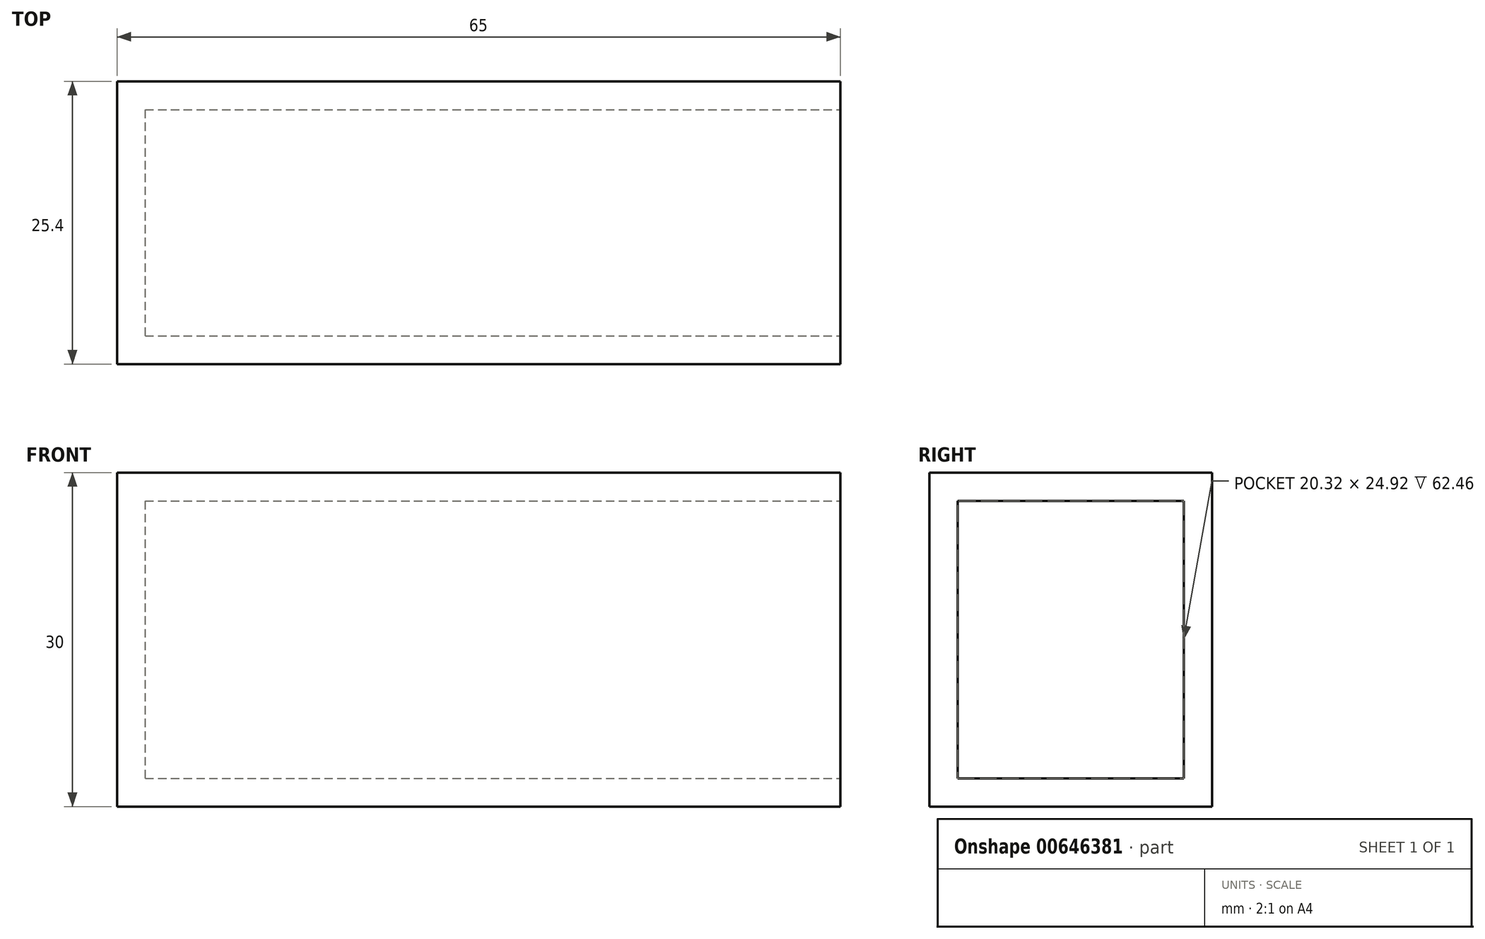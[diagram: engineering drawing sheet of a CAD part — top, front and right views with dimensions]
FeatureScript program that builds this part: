
annotation { "Feature Type Name" : "Feature", "Feature Type Description" : "" }
export const myFeature = defineFeature(function(context is Context, id is Id, definition is map)
    precondition{}
    {
        {
            var Q0;
            Q0=qCreatedBy(makeId("Front.planeOp"),FACE);
            var sketch = newSketch(context, id + "F0", { "sketchPlane" : qUnion([Q0])});
            skLineSegment(sketch, "E0.bottom", {"start": v(-32.5, -15) * mm, "end": v(32.5, -15) * mm});
            skLineSegment(sketch, "E0.top", {"start": v(-32.5, 15) * mm, "end": v(32.5, 15) * mm});
            skLineSegment(sketch, "E0.left", {"start": v(-32.5, -15) * mm, "end": v(-32.5, 15) * mm});
            skLineSegment(sketch, "E0.right", {"start": v(32.5, -15) * mm, "end": v(32.5, 15) * mm});
            skPoint(sketch, "E0.middle", {"position": v(0, 0) * mm});
            skSolve(sketch);
        }
        {
            var Q0;
            Q0=makeQuery(id+"F0.imprint","IMPRINT",FACE,{"disambiguationData":[TD([[makeQuery(id+"F0.imprint","IMPRINT",EDGE,{"derivedFrom":sQuery(id+"F0.wireOp",EDGE,"E0.bottom")}),1.0]])]});
            extrude(context, id + "F1", {"entities" : qUnion([Q0]), "depth" : 25.4 * mm, "offsetDistance" : 25.4 * mm});
        }
        {
            var Q0;
            Q0=makeQuery(id+"F1.opExtrude","SWEPT_FACE",FACE,{"disambiguationData":[OSD([sQuery(id+"F0.wireOp",EDGE,"E0.right")])]});
            shell(context, id + "F2", {"entities" : qUnion([Q0]), "thickness" : 2.54 * mm});
        }
    });
